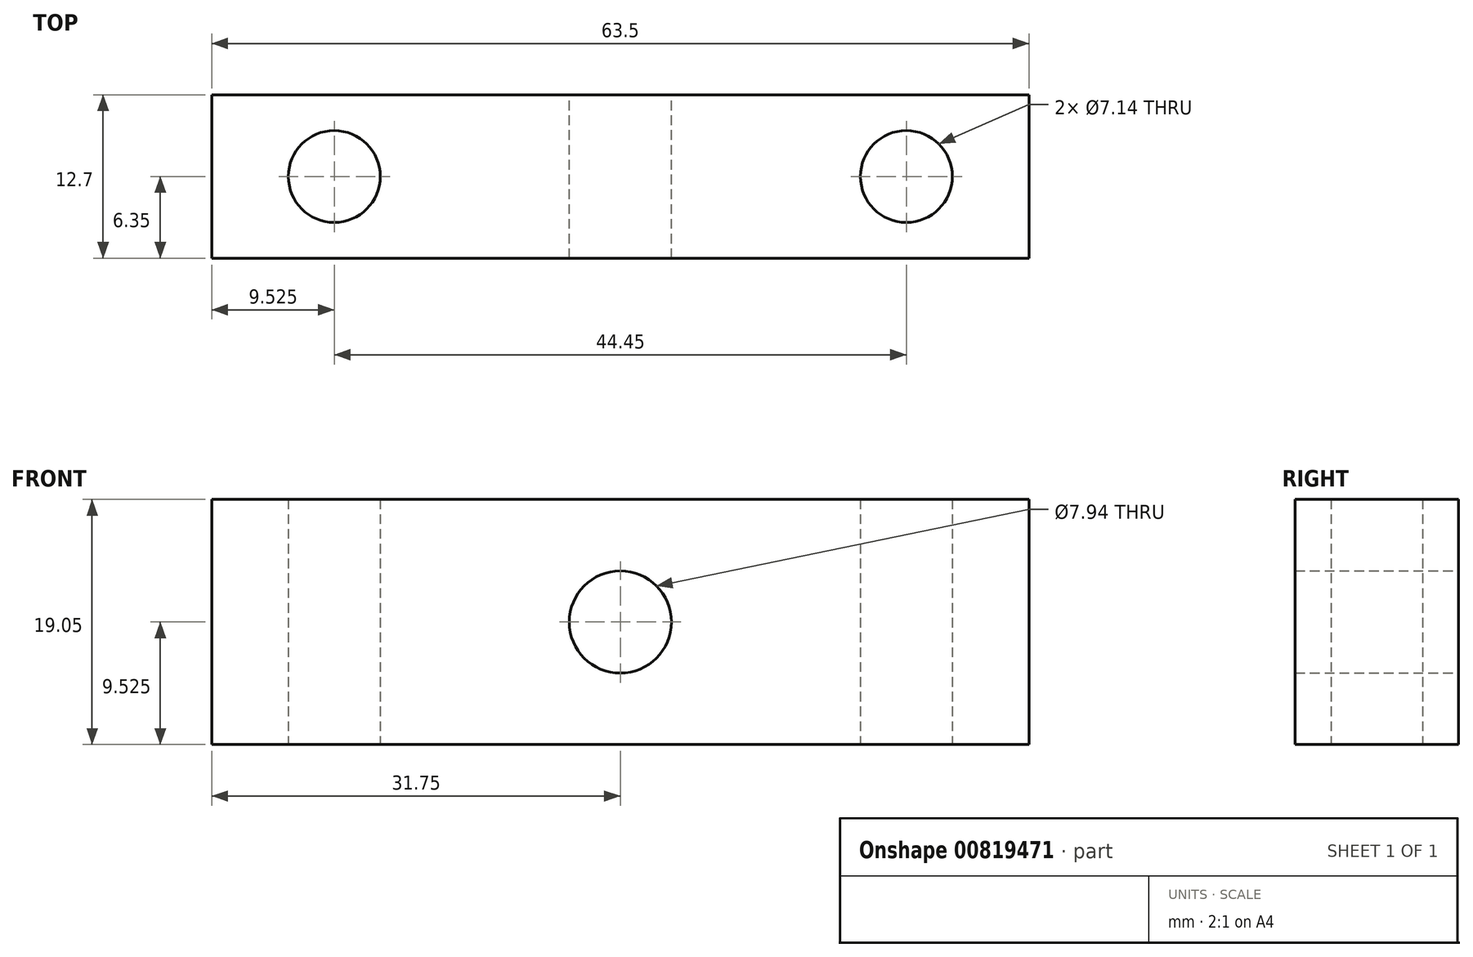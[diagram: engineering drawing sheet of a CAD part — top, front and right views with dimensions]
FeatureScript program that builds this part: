
annotation { "Feature Type Name" : "Feature", "Feature Type Description" : "" }
export const myFeature = defineFeature(function(context is Context, id is Id, definition is map)
    precondition{}
    {
        {
            var Q0;
            Q0=qCreatedBy(makeId("Front.planeOp"),FACE);
            var sketch = newSketch(context, id + "F0", { "sketchPlane" : qUnion([Q0])});
            skLineSegment(sketch, "E0.bottom", {"start": v(-31.75, 0) * mm, "end": v(31.75, 0) * mm});
            skLineSegment(sketch, "E0.top", {"start": v(-31.75, 19.05) * mm, "end": v(31.75, 19.05) * mm});
            skLineSegment(sketch, "E0.left", {"start": v(-31.75, 0) * mm, "end": v(-31.75, 19.05) * mm});
            skLineSegment(sketch, "E0.right", {"start": v(31.75, 0) * mm, "end": v(31.75, 19.05) * mm});
            skLineSegment(sketch, "E1", {"start": v(0, 0) * mm, "end": v(0, 19.05) * mm, "construction": true});
            skPoint(sketch, "E2", {"position": v(0, 9.53) * mm});
            skSolve(sketch);
        }
        {
            var Q0;
            Q0 = qSketchRegion(id + "F0", true);
            extrude(context, id + "F1", {"entities" : qUnion([Q0]), "depth" : 12.7 * mm, "offsetDistance" : 25.4 * mm, "symmetric" : true});
        }
        {
            var Q0;
            Q0=makeQuery(id+"F1.opExtrude","SWEPT_FACE",FACE,{"disambiguationData":[OSD([sQuery(id+"F0.wireOp",EDGE,"E0.top")])]});
            var sketch = newSketch(context, id + "F2", { "sketchPlane" : qUnion([Q0])});
            skLineSegment(sketch, "E3", {"start": v(0, 0) * mm, "end": v(0, 11.93) * mm, "construction": true});
            skPoint(sketch, "E4", {"position": v(-22.22, 0) * mm});
            skPoint(sketch, "E5", {"position": v(22.22, 0) * mm});
            skSolve(sketch);
        }
        {
            var Q0;
            Q0=makeQuery(id+"F1.opExtrude","CAP_FACE",FACE,{"disambiguationData":[OSD([sQuery(id+"F0.wireOp",EDGE,"E0.bottom"),sQuery(id+"F0.wireOp",EDGE,"E0.top"),sQuery(id+"F0.wireOp",EDGE,"E0.left"),sQuery(id+"F0.wireOp",EDGE,"E0.right")])],"isStart":false});
            var sketch = newSketch(context, id + "F3", { "sketchPlane" : qUnion([Q0])});
            skPoint(sketch, "E6", {"position": v(0, 9.53) * mm});
            skSolve(sketch);
        }
        {
            var Q0;
            Q0=sQuery(id+"F3.wireOp",VERTEX,"E6");
            var Q1;
            Q1=makeQuery(id+"F1.opExtrude","SWEPT_BODY",BODY,{"disambiguationData":[OSD([sQuery(id+"F0.wireOp",EDGE,"E0.bottom"),sQuery(id+"F0.wireOp",EDGE,"E0.top"),sQuery(id+"F0.wireOp",EDGE,"E0.left"),sQuery(id+"F0.wireOp",EDGE,"E0.right")])]});
            hole(context, id + "F4", {"style" : HoleStyle.SIMPLE, "endStyle" : HoleEndStyle.THROUGH, "standardTappedOrClearance" : lookupTablePath({ "standard" : "ANSI", "engagement" : "75%", "pitch" : "16 tpi", "size" : "3/8", "type" : "Tapped" }), "standardBlindInLast" : lookupTablePath({ "standard" : "ANSI", "fit" : "Normal", "engagement" : "75%", "pitch" : "16 tpi", "size" : "3/8", "type" : "Clearance & tapped" }), "holeDiameter" : 7.94 * mm, "majorDiameter" : 9.52 * mm, "showTappedDepth" : true, "isTappedThrough" : true, "tappedDepth" : 25.4 * mm, "tapClearance" : 3, "locations" : qUnion([Q0]), "scope" : qUnion([Q1]), "startStyle" : HoleStartStyle.SKETCH});
        }
        {
            var Q0;
            Q0=sQuery(id+"F2.wireOp",VERTEX,"E4");
            var Q1;
            Q1=sQuery(id+"F2.wireOp",VERTEX,"E5");
            var Q2;
            Q2=makeQuery(id+"F1.opExtrude","SWEPT_BODY",BODY,{"disambiguationData":[OSD([sQuery(id+"F0.wireOp",EDGE,"E0.bottom"),sQuery(id+"F0.wireOp",EDGE,"E0.top"),sQuery(id+"F0.wireOp",EDGE,"E0.left"),sQuery(id+"F0.wireOp",EDGE,"E0.right")])]});
            hole(context, id + "F5", {"style" : HoleStyle.SIMPLE, "endStyle" : HoleEndStyle.THROUGH, "standardTappedOrClearance" : lookupTablePath({ "fit" : "Normal (ASME)", "standard" : "ANSI", "size" : "1/4", "type" : "Clearance" }), "standardBlindInLast" : lookupTablePath({ "fit" : "Normal", "standard" : "ANSI", "engagement" : "75%", "pitch" : "20 tpi", "size" : "1/4", "type" : "Clearance & tapped" }), "holeDiameter" : 7.14 * mm, "majorDiameter" : 9.52 * mm, "isTappedThrough" : true, "tappedDepth" : 25.4 * mm, "tapClearance" : 3, "locations" : qUnion([Q0, Q1]), "scope" : qUnion([Q2]), "startStyle" : HoleStartStyle.SKETCH});
        }
    });
